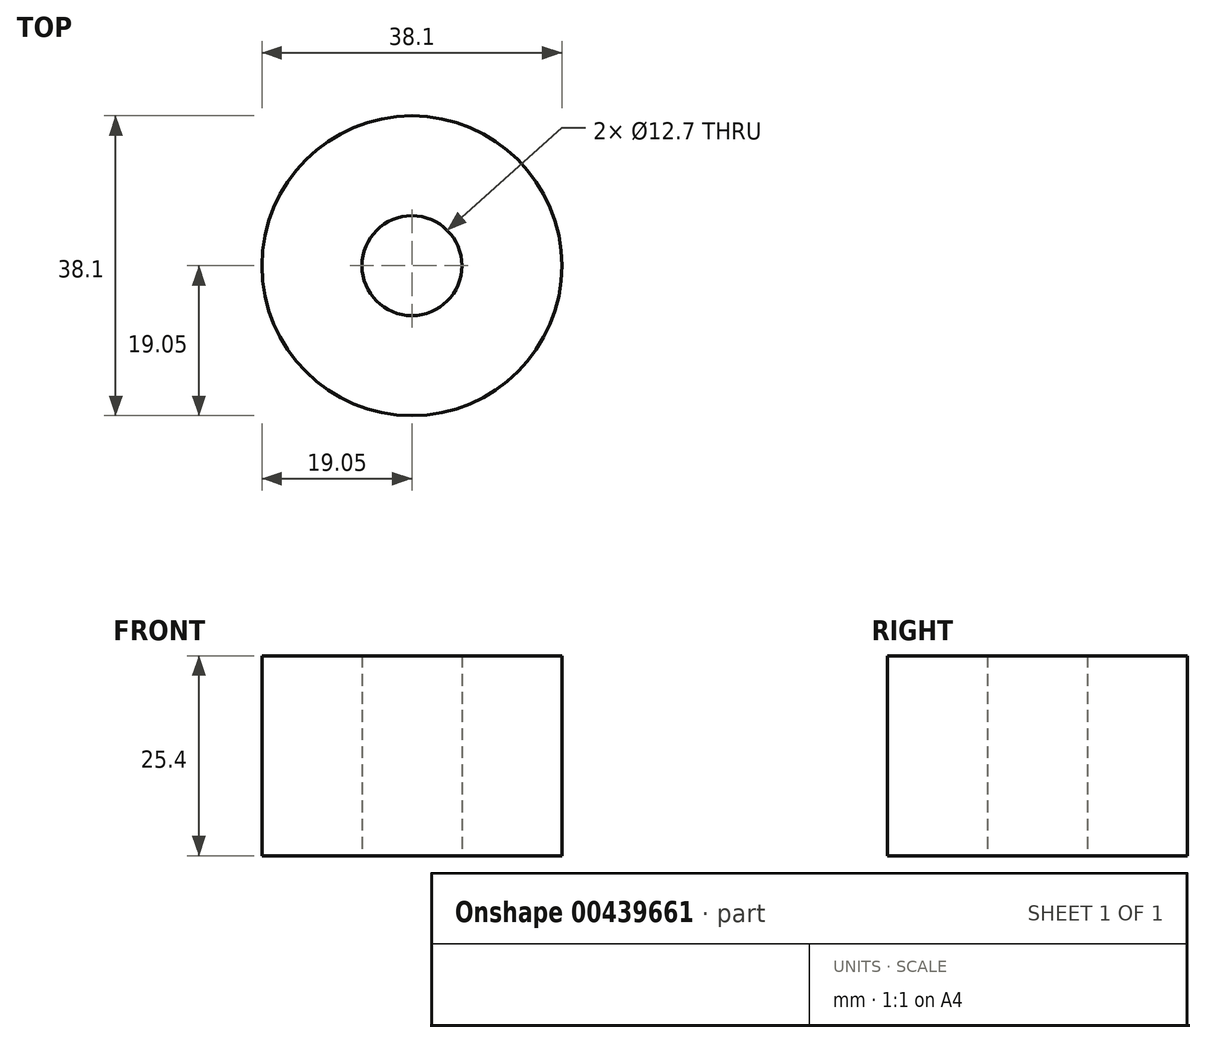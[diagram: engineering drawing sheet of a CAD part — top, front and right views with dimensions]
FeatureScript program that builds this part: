
annotation { "Feature Type Name" : "Feature", "Feature Type Description" : "" }
export const myFeature = defineFeature(function(context is Context, id is Id, definition is map)
    precondition{}
    {
        {
            var Q0;
            Q0=qCreatedBy(makeId("Top.planeOp"),FACE);
            var sketch = newSketch(context, id + "F0", { "sketchPlane" : qUnion([Q0])});
            skCircle(sketch, "E0", {"center": v(0, 0) * mm, "radius": 6.35 * mm});
            skCircle(sketch, "E1", {"center": v(0, 0) * mm, "radius": 19.05 * mm});
            skSolve(sketch);
        }
        {
            var Q0;
            Q0 = qSketchRegion(id + "F0", true);
            extrude(context, id + "F1", {"entities" : qUnion([Q0]), "endBound" : BoundingType.SYMMETRIC, "depth" : 25.4 * mm});
        }
    });
